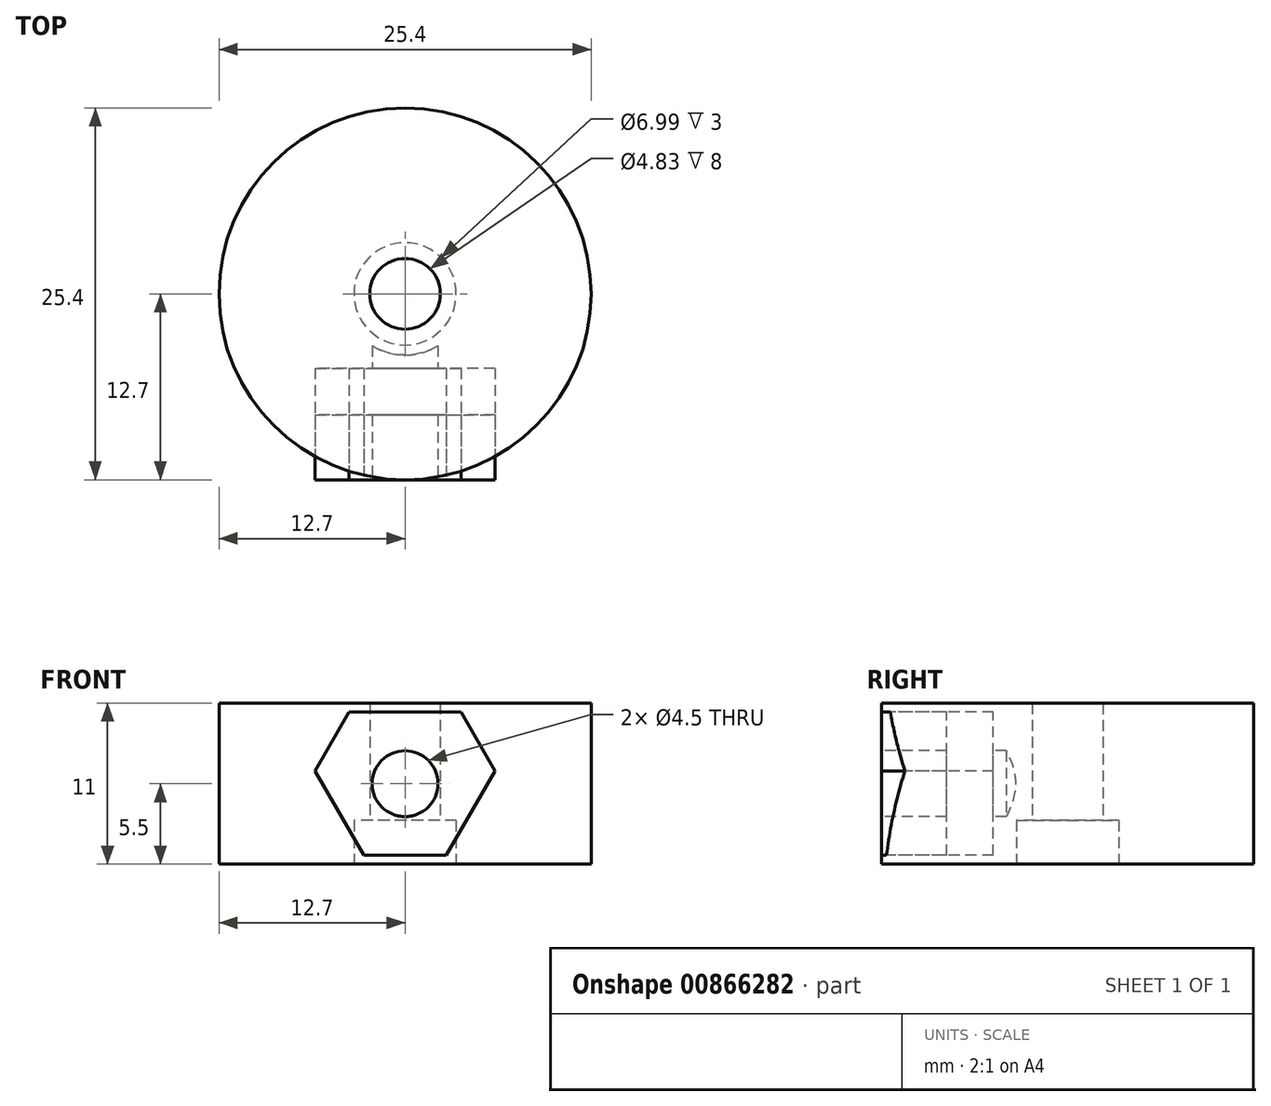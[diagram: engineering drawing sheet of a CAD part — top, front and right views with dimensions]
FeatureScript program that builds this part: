
annotation { "Feature Type Name" : "Feature", "Feature Type Description" : "" }
export const myFeature = defineFeature(function(context is Context, id is Id, definition is map)
    precondition{}
    {
        {
            var Q0;
            Q0=qCreatedBy(makeId("Top.planeOp"),FACE);
            var sketch = newSketch(context, id + "F0", { "sketchPlane" : qUnion([Q0])});
            skCircle(sketch, "E0", {"center": v(0, 0) * mm, "radius": 3.5 * mm});
            skCircle(sketch, "E1", {"center": v(0, 0) * mm, "radius": 12.7 * mm});
            skSolve(sketch);
        }
        {
            var Q0;
            Q0=qSketchRegion(id+"F0",true);
            extrude(context, id + "F1", {"entities" : qUnion([Q0]), "endBound" : BoundingType.SYMMETRIC, "depth" : 11 * mm, "offsetDistance" : 25.4 * mm});
        }
        {
            var Q0;
            Q0=qCreatedBy(makeId("Front.planeOp"),FACE);
            cPlane(context, id + "F2", {"entities" : qUnion([Q0]), "cplaneType" : CPlaneType.OFFSET, "offset" : 12.7 * mm, "width" : 152.4 * mm, "height" : 152.4 * mm});
        }
        {
            var Q0;
            Q0=qCreatedBy(id+"F2.planeOp",FACE);
            var sketch = newSketch(context, id + "F3", { "sketchPlane" : qUnion([Q0])});
            skCircle(sketch, "E2", {"center": v(0, 0) * mm, "radius": 2.25 * mm});
            skSolve(sketch);
        }
        {
            var Q0;
            Q0=makeQuery(id+"F3.imprint","IMPRINT",FACE,{"disambiguationData":[TD([[makeQuery(id+"F3.imprint","IMPRINT",EDGE,{"derivedFrom":sQuery(id+"F3.wireOp",EDGE,"E2")}),1.0]])]});
            extrude(context, id + "F4", {"entities" : qUnion([Q0]), "operationType" : NewBodyOperationType.REMOVE, "oppositeDirection" : true, "depth" : 7.62 * mm, "offsetDistance" : 25.4 * mm});
        }
        {
            var Q0;
            Q0=qCreatedBy(id+"F2.planeOp",FACE);
            var sketch = newSketch(context, id + "F5", { "sketchPlane" : qUnion([Q0])});
            skCircle(sketch, "E3.cCircle", {"center": v(0, 0) * mm, "radius": 4.89 * mm, "construction": true});
            skLineSegment(sketch, "E3.0", {"start": v(2.82, -4.89) * mm, "end": v(-2.82, -4.89) * mm});
            skLineSegment(sketch, "E3.1", {"start": v(-2.82, -4.89) * mm, "end": v(-5.65, 0) * mm});
            skLineSegment(sketch, "E3.2", {"start": v(-5.65, 0) * mm, "end": v(-2.82, 4.89) * mm});
            skLineSegment(sketch, "E3.3", {"start": v(-2.82, 4.89) * mm, "end": v(2.82, 4.89) * mm});
            skLineSegment(sketch, "E3.4", {"start": v(2.82, 4.89) * mm, "end": v(5.65, 0) * mm});
            skLineSegment(sketch, "E3.5", {"start": v(5.65, 0) * mm, "end": v(2.82, -4.89) * mm});
            skPoint(sketch, "E3.0.midPoint", {"position": v(0, -4.89) * mm});
            skLineSegment(sketch, "E4", {"start": v(-5.65, 0) * mm, "end": v(-6.15, 0.87) * mm});
            skLineSegment(sketch, "E5", {"start": v(-6.15, 0.87) * mm, "end": v(-3.82, 4.89) * mm});
            skLineSegment(sketch, "E6", {"start": v(-3.82, 4.89) * mm, "end": v(-2.82, 4.89) * mm});
            skLineSegment(sketch, "E7.MirrorCS", {"start": v(5.65, 0) * mm, "end": v(6.15, 0.87) * mm});
            skLineSegment(sketch, "E8.MirrorCS", {"start": v(3.82, 4.89) * mm, "end": v(2.82, 4.89) * mm});
            skLineSegment(sketch, "E9.MirrorCS", {"start": v(6.15, 0.87) * mm, "end": v(3.82, 4.89) * mm});
            skSolve(sketch);
        }
        {
            var Q0;
            Q0=makeQuery(id+"F5.imprint","IMPRINT",FACE,{"disambiguationData":[TD([[makeQuery(id+"F5.imprint","IMPRINT",EDGE,{"derivedFrom":sQuery(id+"F5.wireOp",EDGE,"E3.2")}),1.0]])]});
            var Q1;
            Q1=makeQuery(id+"F5.imprint","IMPRINT",FACE,{"disambiguationData":[TD([[makeQuery(id+"F5.imprint","IMPRINT",EDGE,{"derivedFrom":sQuery(id+"F5.wireOp",EDGE,"E3.0")}),-1.0]])]});
            var Q2;
            Q2=makeQuery(id+"F5.imprint","IMPRINT",FACE,{"disambiguationData":[TD([[makeQuery(id+"F5.imprint","IMPRINT",EDGE,{"derivedFrom":sQuery(id+"F5.wireOp",EDGE,"E3.4")}),1.0]])]});
            extrude(context, id + "F6", {"entities" : qUnion([Q0, Q1, Q2]), "operationType" : NewBodyOperationType.REMOVE, "oppositeDirection" : true, "depth" : 7.62 * mm, "offsetDistance" : 25.4 * mm});
        }
        {
            var Q0;
            Q0=qSketchRegion(id+"F5",true);
            extrude(context, id + "F7", {"entities" : qUnion([Q0]), "oppositeDirection" : true, "depth" : 7.62 * mm - 3.2 * mm, "offsetDistance" : 25.4 * mm});
        }
        {
            var Q0;
            Q0=qSketchRegion(id+"F3",true);
            extrude(context, id + "F8", {"entities" : qUnion([Q0]), "operationType" : NewBodyOperationType.REMOVE, "oppositeDirection" : true, "depth" : 12.7 * mm, "offsetDistance" : 25.4 * mm});
        }
        {
            var Q0;
            Q0=qCreatedBy(makeId("Top.planeOp"),FACE);
            var sketch = newSketch(context, id + "F9", { "sketchPlane" : qUnion([Q0])});
            skCircle(sketch, "E10", {"center": v(0, 0) * mm, "radius": 2.41 * mm});
            skCircle(sketch, "E11", {"center": v(0, 0) * mm, "radius": 4.19 * mm});
            skSolve(sketch);
        }
        {
            var Q0;
            Q0=makeQuery(id+"F9.imprint","IMPRINT",FACE,{"disambiguationData":[TD([[makeQuery(id+"F9.imprint","IMPRINT",EDGE,{"derivedFrom":sQuery(id+"F9.wireOp",EDGE,"E10")}),-1.0]])]});
            extrude(context, id + "F10", {"entities" : qUnion([Q0]), "operationType" : NewBodyOperationType.ADD, "depth" : 5.5 * mm, "offsetDistance" : 25.4 * mm, "hasSecondDirection" : true, "secondDirectionOppositeDirection" : true, "secondDirectionDepth" : 2.5 * mm});
        }
        {
            var Q0;
            Q0=qCreatedBy(id+"F2.planeOp",FACE);
            cPlane(context, id + "F11", {"entities" : qUnion([Q0]), "cplaneType" : CPlaneType.OFFSET, "offset" : 25.4 * mm, "oppositeDirection" : true, "width" : 152.4 * mm, "height" : 152.4 * mm});
        }
    });
